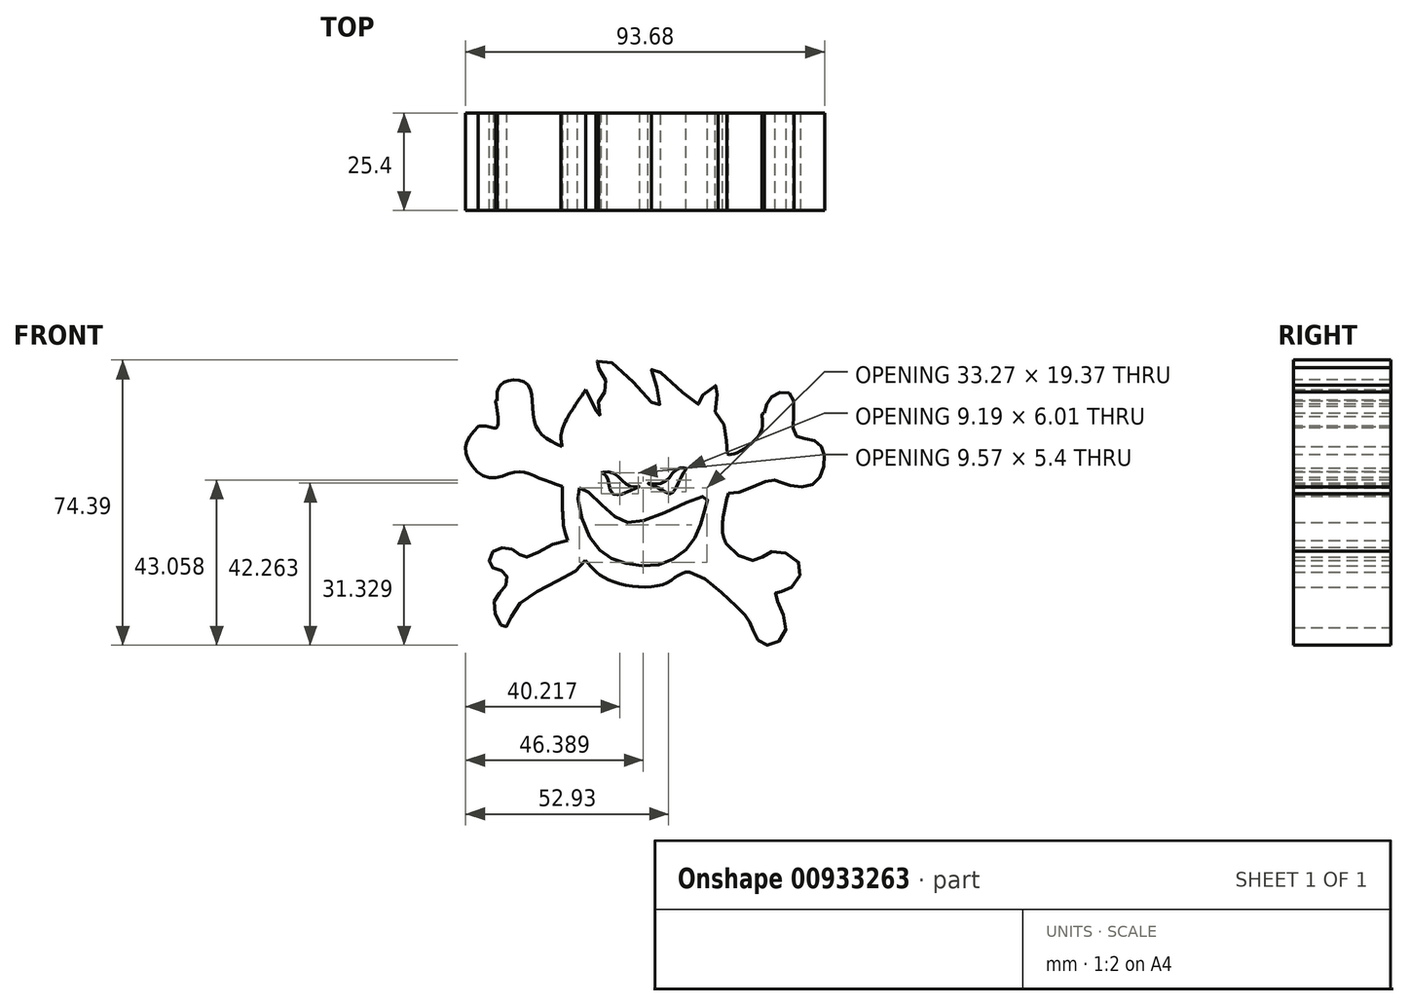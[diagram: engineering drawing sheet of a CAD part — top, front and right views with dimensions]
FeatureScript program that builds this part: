
annotation { "Feature Type Name" : "Feature", "Feature Type Description" : "" }
export const myFeature = defineFeature(function(context is Context, id is Id, definition is map)
    precondition{}
    {
        {
            var Q0;
            Q0=qCreatedBy(makeId("Front.planeOp"),FACE);
            var sketch = newSketch(context, id + "F0", { "sketchPlane" : qUnion([Q0])});
            skFitSpline(sketch, "E0", {"points": [v(-28.1, 3.44) * mm, v(-29.43, 6.9) * mm, v(-29.99, 18.5) * mm], "startDerivative": vector(-4.22, 8.03) * mm, "endDerivative": vector(0.03, 20.9) * mm});
            skFitSpline(sketch, "E1", {"points": [v(-29.99, 18.5) * mm, v(-36.91, 21.03) * mm, v(-41.8, 22.29) * mm, v(-49.54, 20.87) * mm, v(-55.22, 27.81) * mm, v(-52, 34.1) * mm], "startDerivative": vector(-36.23, 12.24) * mm, "endDerivative": vector(25.89, 28.97) * mm});
            skFitSpline(sketch, "E2", {"points": [v(-52, 34.1) * mm, v(-49.54, 34.1) * mm, v(-46.93, 34.1) * mm, v(-47.32, 40.82) * mm, v(-47.06, 40.82) * mm], "startDerivative": vector(9.03, 1.33) * mm, "endDerivative": vector(4, -2.07) * mm});
            skFitSpline(sketch, "E3", {"points": [v(-47.06, 40.82) * mm, v(-45.73, 45.33) * mm, v(-39.1, 45.06) * mm, v(-37.1, 34.71) * mm, v(-30.07, 28.87) * mm], "startDerivative": vector(-0.09, 26.6) * mm, "endDerivative": vector(32.68, -15.53) * mm});
            skFitSpline(sketch, "E4", {"points": [v(-30.07, 28.87) * mm, v(-29.99, 18.5) * mm], "startDerivative": vector(0.08, -10.37) * mm, "endDerivative": vector(0.08, -10.37) * mm});
            skFitSpline(sketch, "E5", {"points": [v(-30.07, 28.87) * mm, v(-30.07, 33.12) * mm, v(-23.83, 43.74) * mm], "startDerivative": vector(-1.83, 10.48) * mm, "endDerivative": vector(13.02, 18.54) * mm});
            skFitSpline(sketch, "E6", {"points": [v(-23.83, 43.74) * mm, v(-20.25, 36.7) * mm, v(-20.52, 40.82) * mm, v(-18.66, 43.74) * mm, v(-19.46, 47.98) * mm, v(-21.27, 50.7) * mm, v(-17.05, 50.7) * mm, v(-5.04, 39.25) * mm, v(-5.41, 44.7) * mm, v(-6.35, 49.48) * mm, v(5.29, 39.9) * mm, v(6.32, 41.8) * mm, v(10.5, 44.75) * mm, v(9.75, 38.56) * mm, v(12.9, 33.02) * mm, v(13.08, 26.92) * mm, v(21.66, 32.46) * mm, v(22.18, 37.37) * mm, v(22.74, 37.7) * mm], "startDerivative": vector(77.83, -168.26) * mm, "endDerivative": vector(36.99, 7.73) * mm});
            skFitSpline(sketch, "E7", {"points": [v(22.74, 37.7) * mm, v(25.01, 42.22) * mm, v(29.9, 42.14) * mm, v(30.53, 32.2) * mm, v(35.58, 30.46) * mm, v(38.42, 26.05) * mm, v(35.35, 19.02) * mm, v(27.7, 19.26) * mm, v(23.9, 20.05) * mm, v(13.33, 16.66) * mm, v(13.08, 26.92) * mm], "startDerivative": vector(13.88, 60.87) * mm, "endDerivative": vector(23.1, 116.85) * mm});
            skFitSpline(sketch, "E8", {"points": [v(-23.96, -0.8) * mm, v(-18.12, -5.78) * mm, v(-3.5, -7) * mm, v(3.2, -3.88) * mm, v(15.58, -13.03) * mm, v(18.7, -16.49) * mm, v(20.04, -19.84) * mm, v(23.18, -22.93) * mm, v(28.25, -19.36) * mm, v(25.9, -10.92) * mm, v(25.8, -9.13) * mm, v(28.81, -8.57) * mm, v(32.1, -2.2) * mm, v(24.68, 1.47) * mm, v(20.74, -0.8) * mm, v(12.86, 3.44) * mm, v(13.33, 16.66) * mm], "startDerivative": vector(67.63, -83.29) * mm, "endDerivative": vector(44.45, 170.04) * mm});
            skFitSpline(sketch, "E9", {"points": [v(3.2, -3.88) * mm, v(12.86, 3.44) * mm], "startDerivative": vector(9.67, 7.32) * mm, "endDerivative": vector(9.67, 7.32) * mm});
            skFitSpline(sketch, "E10", {"points": [v(-19.8, 22.01) * mm, v(-16.8, 22.01) * mm, v(-12.38, 18.5) * mm, v(-9.86, 18.5) * mm, v(-12.38, 17.36) * mm, v(-13.88, 16.66) * mm, v(-16.96, 16.66) * mm, v(-18.54, 21.3) * mm, v(-19.8, 22.01) * mm]});
            skFitSpline(sketch, "E11", {"points": [v(2.3, 23.12) * mm, v(0, 22.96) * mm, v(-3.94, 19.33) * mm, v(-7.65, 19.33) * mm, v(-4.17, 17.67) * mm, v(-1.41, 16.66) * mm, v(1.59, 22.01) * mm, v(2.3, 23.12) * mm]});
            skFitSpline(sketch, "E12", {"points": [v(-2.75, 18.5) * mm, v(0, 20.83) * mm, v(-1.1, 18.5) * mm, v(-2.75, 18.5) * mm]});
            skFitSpline(sketch, "E13", {"points": [v(-16.88, 20.04) * mm, v(-14.27, 18.5) * mm, v(-14.51, 17.67) * mm, v(-16.88, 20.04) * mm]});
            skFitSpline(sketch, "E14", {"points": [v(-25.48, 18.07) * mm, v(-17.75, 11.75) * mm, v(-8.67, 9.54) * mm, v(7.5, 15.86) * mm, v(7.27, 12.54) * mm, v(4.03, 4.1) * mm, v(-4.33, -1.82) * mm, v(-15.7, -0.87) * mm, v(-23.2, 5.91) * mm, v(-25.48, 18.07) * mm]});
            skFitSpline(sketch, "E15", {"points": [v(-23.5, 13.4) * mm, v(-15.62, 8.75) * mm, v(-3.94, 8.91) * mm, v(5.14, 12.38) * mm, v(4.58, 7.41) * mm, v(0.8, 1.5) * mm, v(-7.1, -1.03) * mm, v(-15.7, 0) * mm, v(-21.3, 5.2) * mm, v(-24.3, 11.12) * mm, v(-23.5, 13.4) * mm]});
            skFitSpline(sketch, "E16", {"points": [v(-21.66, 11.46) * mm, v(-19.97, 10.52) * mm, v(-21.85, 7.6) * mm, v(-21.66, 7.7) * mm], "startDerivative": vector(7, -1.07) * mm, "endDerivative": vector(2.37, 1.6) * mm});
            skFitSpline(sketch, "E17", {"points": [v(-21.76, 7.64) * mm, v(-21.66, 11.46) * mm], "startDerivative": vector(0.1, 3.82) * mm, "endDerivative": vector(0.1, 3.82) * mm});
            skFitSpline(sketch, "E18", {"points": [v(-19.39, 10.11) * mm, v(-19.5, 8.55) * mm, v(-18.33, 2.91) * mm, v(-21.66, 6.32) * mm, v(-19.39, 10.11) * mm]});
            skFitSpline(sketch, "E19", {"points": [v(-18.22, 9.78) * mm, v(-18.27, 7.64) * mm, v(-16.99, 2.3) * mm, v(-16.04, 5.03) * mm, v(-13.57, 7.96) * mm, v(-18.22, 9.78) * mm]});
            skFitSpline(sketch, "E20", {"points": [v(-12.96, 7.8) * mm, v(-13.7, 6.6) * mm, v(-15.87, 3.58) * mm, v(-15.43, 0.51) * mm, v(-10.46, -0.43) * mm, v(-12.96, 7.8) * mm]});
            skFitSpline(sketch, "E21", {"points": [v(-11.69, 8.05) * mm, v(-7.19, 7.87) * mm, v(-8.34, 1.24) * mm, v(-8.9, 0.46) * mm, v(-8.9, 0) * mm, v(-9, 0) * mm], "startDerivative": vector(18.33, 4.76) * mm, "endDerivative": vector(-2.76, 0.87) * mm});
            skFitSpline(sketch, "E22", {"points": [v(-11.69, 8.05) * mm, v(-8.9, 0) * mm], "startDerivative": vector(2.79, -8.05) * mm, "endDerivative": vector(2.79, -8.05) * mm});
            skFitSpline(sketch, "E23", {"points": [v(-8.45, -0.43) * mm, v(-7.61, 0.46) * mm, v(-6.05, 7.49) * mm], "startDerivative": vector(2.96, 2.06) * mm, "endDerivative": vector(1.97, 12.36) * mm});
            skFitSpline(sketch, "E24", {"points": [v(-6.05, 7.49) * mm, v(-2.76, 2.8) * mm, v(-2.43, 0.46) * mm], "startDerivative": vector(6.8, -8.22) * mm, "endDerivative": vector(-0.04, -5.65) * mm});
            skFitSpline(sketch, "E25", {"points": [v(-2.48, 0.57) * mm, v(-8.45, -0.43) * mm], "startDerivative": vector(-5.97, -1) * mm, "endDerivative": vector(-5.97, -1) * mm});
            skFitSpline(sketch, "E26", {"points": [v(-4.94, 8.53) * mm, v(-0.7, 9.1) * mm, v(-1.59, 2.7) * mm], "startDerivative": vector(11.95, 4.14) * mm, "endDerivative": vector(-4.68, -15.19) * mm});
            skFitSpline(sketch, "E27", {"points": [v(-1.59, 2.7) * mm, v(-5.48, 8.35) * mm], "startDerivative": vector(-3.9, 5.66) * mm, "endDerivative": vector(-3.9, 5.66) * mm});
            skFitSpline(sketch, "E28", {"points": [v(-4.94, 8.53) * mm, v(-5.48, 8.35) * mm], "startDerivative": vector(-0.54, -0.19) * mm, "endDerivative": vector(-0.54, -0.19) * mm});
            skFitSpline(sketch, "E29", {"points": [v(-1.07, 2.1) * mm, v(0, 5.8) * mm, v(0, 8.64) * mm, v(1.77, 4.74) * mm], "startDerivative": vector(4.3, 9.83) * mm, "endDerivative": vector(6.53, -16.65) * mm});
            skFitSpline(sketch, "E30", {"points": [v(-1.07, 2.1) * mm, v(1.2, 3.65) * mm, v(1.18, 3.65) * mm, v(1.18, 3.65) * mm], "startDerivative": vector(3.79, 2.55) * mm, "endDerivative": vector(-0.1, -0.15) * mm});
            skFitSpline(sketch, "E31", {"points": [v(1.2, 3.65) * mm, v(1.77, 4.74) * mm], "startDerivative": vector(0.58, 1.08) * mm, "endDerivative": vector(0.58, 1.08) * mm});
            skFitSpline(sketch, "E32", {"points": [v(2.37, 6.51) * mm, v(0.7, 9.66) * mm, v(2.23, 10.6) * mm], "startDerivative": vector(-4.74, 6.3) * mm, "endDerivative": vector(5.03, 1.59) * mm});
            skFitSpline(sketch, "E33", {"points": [v(2.23, 10.6) * mm, v(2.37, 6.51) * mm], "startDerivative": vector(0.13, -4.08) * mm, "endDerivative": vector(0.13, -4.08) * mm});
            skFitSpline(sketch, "E34", {"points": [v(3.26, 10.6) * mm, v(3.43, 7) * mm, v(4.69, 9.23) * mm, v(3.26, 10.6) * mm]});
            skFitSpline(sketch, "E35", {"points": [v(-28.6, 4.4) * mm, v(-39.34, 0) * mm, v(-42.55, 1.8) * mm, v(-47.68, 1.8) * mm, v(-48.75, -2.27) * mm, v(-45.12, -3.98) * mm, v(-44.9, -7.62) * mm, v(-47.9, -12.1) * mm, v(-45.12, -18.31) * mm, v(-41.26, -12.32) * mm, v(-23.96, -0.8) * mm, v(-28.6, 4.4) * mm]});
            skSolve(sketch);
        }
        {
            var Q0;
            Q0 = qSketchRegion(id + "F0", true);
            extrude(context, id + "F1", {"entities" : qUnion([Q0]), "depth" : 25.4 * mm, "offsetDistance" : 25.4 * mm});
        }
        {
            var Q0;
            Q0 = qSketchRegion(id + "F0", true);
            extrude(context, id + "F2", {"entities" : qUnion([Q0]), "operationType" : NewBodyOperationType.ADD, "depth" : 25.4 * mm, "offsetDistance" : 25.4 * mm});
        }
    });
